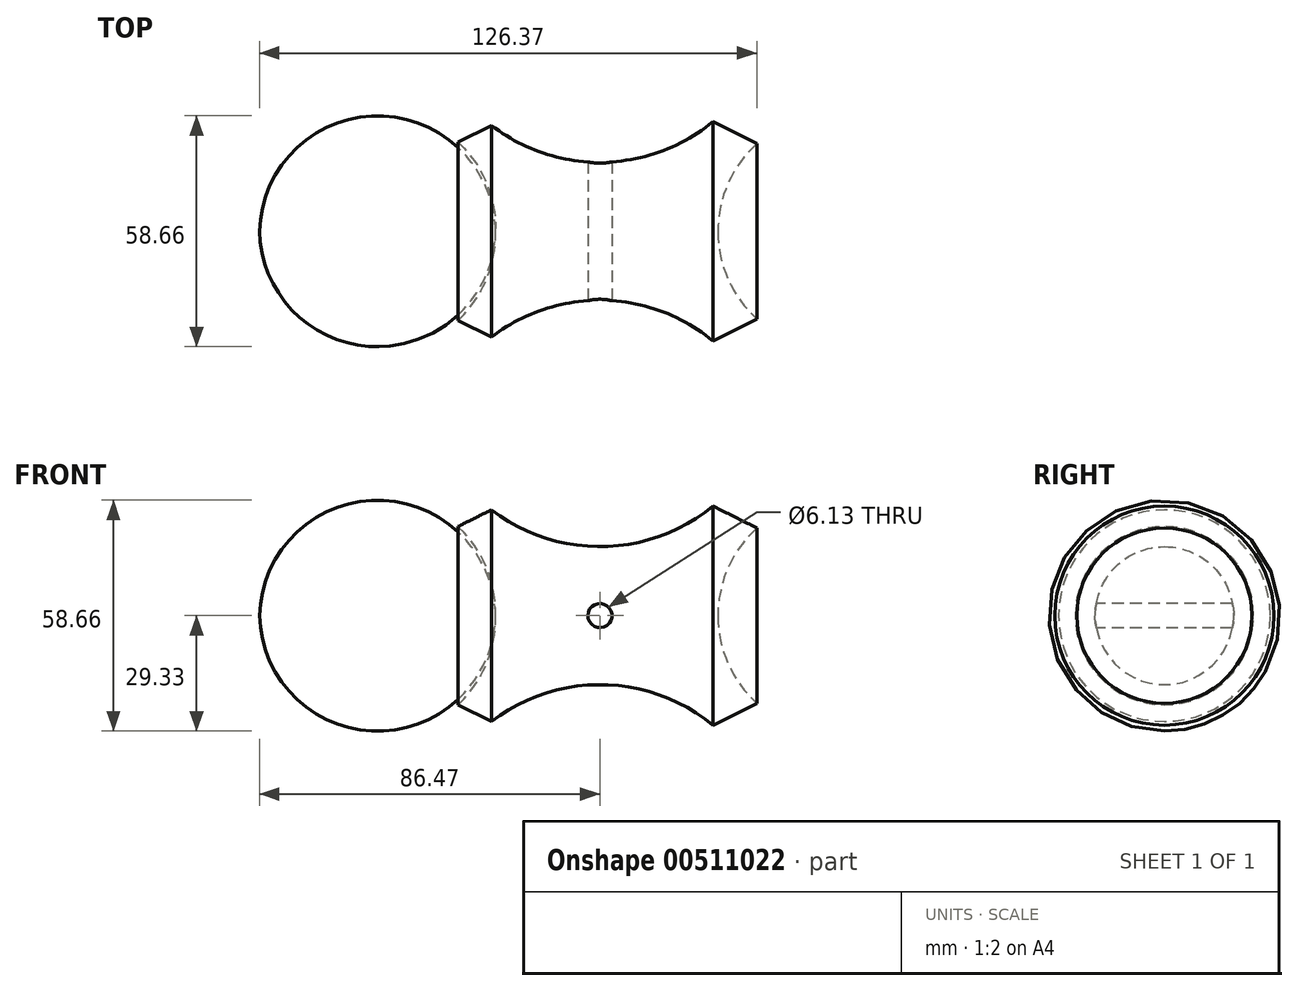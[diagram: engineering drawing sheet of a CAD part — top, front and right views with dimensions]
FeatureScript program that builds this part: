
annotation { "Feature Type Name" : "Feature", "Feature Type Description" : "" }
export const myFeature = defineFeature(function(context is Context, id is Id, definition is map)
    precondition{}
    {
        {
            var Q0;
            Q0=qCreatedBy(makeId("Front.planeOp"),FACE);
            var sketch = newSketch(context, id + "F0", { "sketchPlane" : qUnion([Q0])});
            skLineSegment(sketch, "E0", {"start": v(0, 40.98) * mm, "end": v(0, -19.48) * mm, "construction": true});
            skLineSegment(sketch, "E1", {"start": v(-26.48, 0) * mm, "end": v(30, 0) * mm});
            skArc(sketch, "E2", {"start": v(39.9, 22.27) * mm, "mid": v(32.59, 12.18) * mm, "end": v(30, 0) * mm});
            skPoint(sketch, "E3", {"position": v(0, 0) * mm});
            skPoint(sketch, "E4", {"position": v(-60, 0) * mm});
            skPoint(sketch, "E5.orphan", {"position": v(-35, 0) * mm});
            skPoint(sketch, "E6.orphan", {"position": v(35, 0) * mm});
            skArc(sketch, "E7", {"start": v(-27.54, 26.88) * mm, "mid": v(0.76, 17.55) * mm, "end": v(28.74, 27.83) * mm});
            skLineSegment(sketch, "E8", {"start": v(-36.04, 22.64) * mm, "end": v(-27.54, 26.88) * mm});
            skLineSegment(sketch, "E9.MirrorCS", {"start": v(-43.94, 73.65) * mm, "end": v(-48.07, 76.75) * mm, "construction": true});
            skPoint(sketch, "E10.orphan", {"position": v(0.27, 40.43) * mm});
            skLineSegment(sketch, "E11", {"start": v(-96.35, 19.48) * mm, "end": v(-82.82, 19.48) * mm});
            skLineSegment(sketch, "E12", {"start": v(39.9, 22.27) * mm, "end": v(28.74, 27.83) * mm});
            skLineSegment(sketch, "E13.trimOffspring", {"start": v(-20.04, 22.22) * mm, "end": v(-35.87, 22.72) * mm});
            skArc(sketch, "E14.trimOffspring", {"start": v(-26.48, 0) * mm, "mid": v(-28.84, 12.34) * mm, "end": v(-36.04, 22.64) * mm});
            skSolve(sketch);
        }
        {
            var Q0;
            Q0 = qSketchRegion(id + "F0", true);
            var Q1;
            Q1=sQuery(id+"F0.wireOp",EDGE,"E1");
            revolve(context, id + "F1", {"entities" : qUnion([Q0]), "axis" : qUnion([Q1]), "revolveType" : RevolveType.FULL});
        }
        {
            var Q0;
            Q0=qCreatedBy(makeId("Front.planeOp"),FACE);
            var sketch = newSketch(context, id + "F2", { "sketchPlane" : qUnion([Q0])});
            skCircle(sketch, "E15", {"center": v(0, 0) * mm, "radius": 3.06 * mm});
            skSolve(sketch);
        }
        {
            var Q0;
            Q0 = qSketchRegion(id + "F2", true);
            extrude(context, id + "F3", {"entities" : qUnion([Q0]), "operationType" : NewBodyOperationType.REMOVE, "oppositeDirection" : true, "depth" : 37.8 * mm, "offsetDistance" : 25 * mm, "symmetric" : true});
        }
    });
